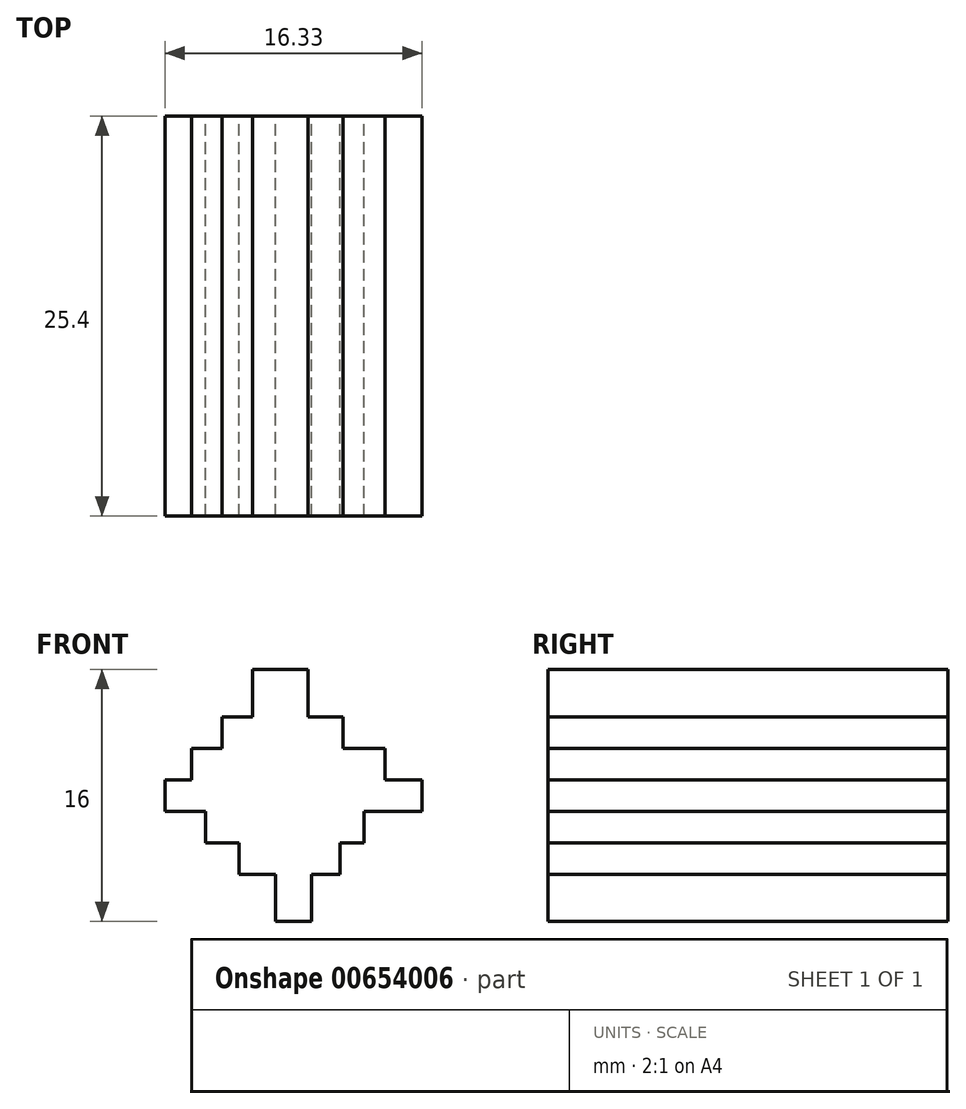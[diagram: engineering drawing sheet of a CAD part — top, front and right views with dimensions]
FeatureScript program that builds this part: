
annotation { "Feature Type Name" : "Feature", "Feature Type Description" : "" }
export const myFeature = defineFeature(function(context is Context, id is Id, definition is map)
    precondition{}
    {
        {
            var Q0;
            Q0=qCreatedBy(makeId("Front.planeOp"),FACE);
            var sketch = newSketch(context, id + "F0", { "sketchPlane" : qUnion([Q0])});
            skLineSegment(sketch, "E0", {"start": v(-10.22, 0) * mm, "end": v(-10.22, 2) * mm});
            skLineSegment(sketch, "E1", {"start": v(-10.22, 2) * mm, "end": v(-8.52, 2) * mm});
            skLineSegment(sketch, "E2", {"start": v(-8.52, 2) * mm, "end": v(-8.52, 4) * mm});
            skLineSegment(sketch, "E3", {"start": v(-8.52, 4) * mm, "end": v(-6.6, 4) * mm});
            skLineSegment(sketch, "E4", {"start": v(-6.6, 4) * mm, "end": v(-6.6, 6) * mm});
            skLineSegment(sketch, "E5", {"start": v(-6.6, 6) * mm, "end": v(-4.65, 6) * mm});
            skLineSegment(sketch, "E6", {"start": v(-4.65, 6) * mm, "end": v(-4.65, 9) * mm});
            skLineSegment(sketch, "E7", {"start": v(-4.65, 9) * mm, "end": v(-1.14, 9) * mm});
            skLineSegment(sketch, "E8", {"start": v(-1.14, 9) * mm, "end": v(-1.14, 6) * mm});
            skLineSegment(sketch, "E9", {"start": v(-1.14, 6) * mm, "end": v(1.1, 6) * mm});
            skLineSegment(sketch, "E10", {"start": v(1.1, 6) * mm, "end": v(1.1, 4) * mm});
            skLineSegment(sketch, "E11", {"start": v(1.1, 4) * mm, "end": v(3.75, 4) * mm});
            skLineSegment(sketch, "E12", {"start": v(3.75, 4) * mm, "end": v(3.75, 2) * mm});
            skLineSegment(sketch, "E13", {"start": v(3.75, 2) * mm, "end": v(6.11, 2) * mm});
            skLineSegment(sketch, "E14", {"start": v(6.11, 2) * mm, "end": v(6.11, 0) * mm});
            skLineSegment(sketch, "E15", {"start": v(6.11, 0) * mm, "end": v(2.42, 0) * mm});
            skLineSegment(sketch, "E16", {"start": v(2.42, 0) * mm, "end": v(2.42, -2) * mm});
            skLineSegment(sketch, "E17", {"start": v(2.42, -2) * mm, "end": v(0.9, -2) * mm});
            skLineSegment(sketch, "E18", {"start": v(0.9, -2) * mm, "end": v(0.9, -4) * mm});
            skLineSegment(sketch, "E19", {"start": v(0.9, -4) * mm, "end": v(-0.92, -4) * mm});
            skLineSegment(sketch, "E20", {"start": v(-0.92, -4) * mm, "end": v(-0.92, -7) * mm});
            skLineSegment(sketch, "E21", {"start": v(-0.92, -7) * mm, "end": v(-3.2, -7) * mm});
            skLineSegment(sketch, "E22", {"start": v(-3.2, -7) * mm, "end": v(-3.2, -4) * mm});
            skLineSegment(sketch, "E23", {"start": v(-3.2, -4) * mm, "end": v(-5.51, -4) * mm});
            skLineSegment(sketch, "E24", {"start": v(-5.51, -4) * mm, "end": v(-5.51, -2) * mm});
            skLineSegment(sketch, "E25", {"start": v(-5.51, -2) * mm, "end": v(-7.66, -2) * mm});
            skLineSegment(sketch, "E26", {"start": v(-7.66, -2) * mm, "end": v(-7.66, 0) * mm});
            skLineSegment(sketch, "E27", {"start": v(-7.66, 0) * mm, "end": v(-10.22, 0) * mm});
            skSolve(sketch);
        }
        {
            var Q0;
            Q0=makeQuery(id+"F0.imprint","IMPRINT",FACE,{"disambiguationData":[TD([[makeQuery(id+"F0.imprint","IMPRINT",EDGE,{"derivedFrom":sQuery(id+"F0.wireOp",EDGE,"E0")}),-1.0]])]});
            extrude(context, id + "F1", {"entities" : qUnion([Q0]), "depth" : 25.4 * mm, "offsetDistance" : 25.4 * mm});
        }
    });
